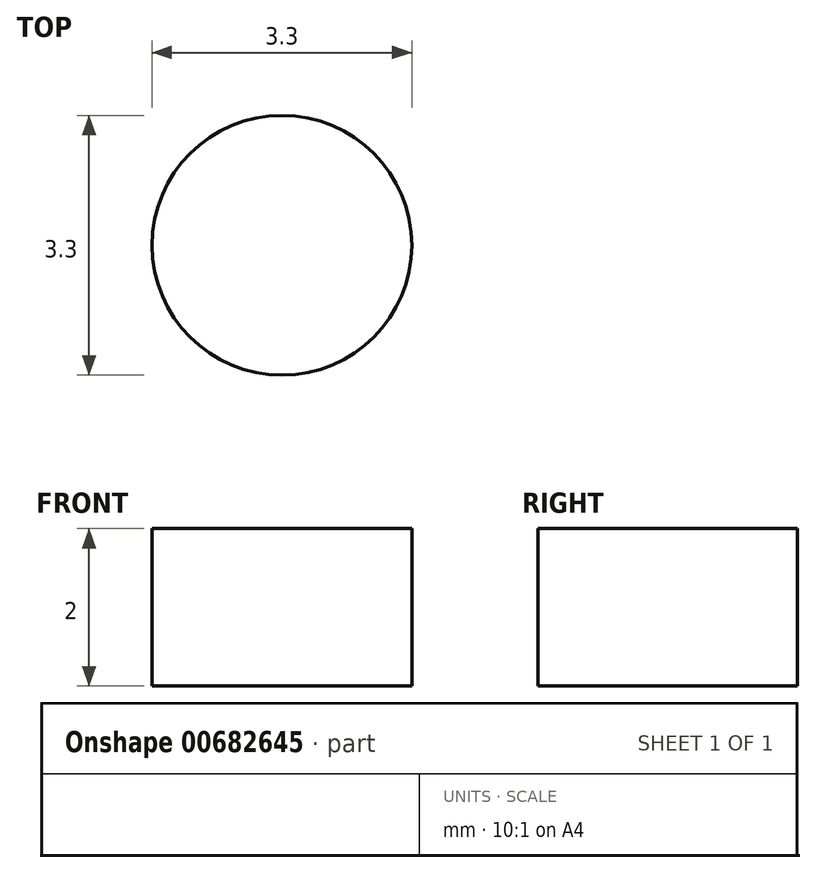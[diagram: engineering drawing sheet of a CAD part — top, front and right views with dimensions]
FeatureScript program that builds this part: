
annotation { "Feature Type Name" : "Feature", "Feature Type Description" : "" }
export const myFeature = defineFeature(function(context is Context, id is Id, definition is map)
    precondition{}
    {
        {
            var Q0;
            Q0=qCreatedBy(makeId("Top.planeOp"),FACE);
            var sketch = newSketch(context, id + "F0", { "sketchPlane" : qUnion([Q0])});
            skCircle(sketch, "E0", {"center": v(0, 0) * mm, "radius": 1.65 * mm});
            skSolve(sketch);
        }
        {
            var Q0;
            Q0=makeQuery(id+"F0.imprint","IMPRINT",FACE,{"disambiguationData":[TD([[makeQuery(id+"F0.imprint","IMPRINT",EDGE,{"derivedFrom":sQuery(id+"F0.wireOp",EDGE,"E0")}),1.0]])]});
            extrude(context, id + "F1", {"entities" : qUnion([Q0]), "depth" : 2 * mm, "offsetDistance" : 25.4 * mm});
        }
    });
